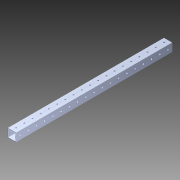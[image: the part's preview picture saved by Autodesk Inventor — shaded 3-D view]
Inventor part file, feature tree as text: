
AUTODESK INVENTOR PART (.ipt)
format: ipt  version: 2014 SP1 (Build 180222100, 222)  size: 1,286,144 bytes
history: native  units: in
note: dims shown in document units (in); Inventor stores cm internally (conversion verified against a paired STEP export)
features: extrude x2, sketch x2, pattern_circular x1, other x1, imported_body x1
ambient origin geometry x8: Origin, YZ Plane, XZ Plane, XY Plane, X Axis, Y Axis, Z Axis, Center Point
bodies: Body1 (feature_tree)
feature tree (7):
  pattern_circular  "CirPattern2"
  other  "1x1 tube1"
  extrude  "Extrusion1"  Depth=1.0in TaperAngle=0.0deg
  extrude  "Extrusion2"  [1 undecoded]
  imported_body  "Base1"
  sketch  "Sketch1"  dims[d0=39.0in d1=0.0in d2=1.0in d3=0.0in]
  sketch  "Sketch3"
note: 1 required parameter value undecoded (feature->parameter linkage not recoverable at this tier; creation-order binding heuristic only, values carry confidence <= 0.55)
